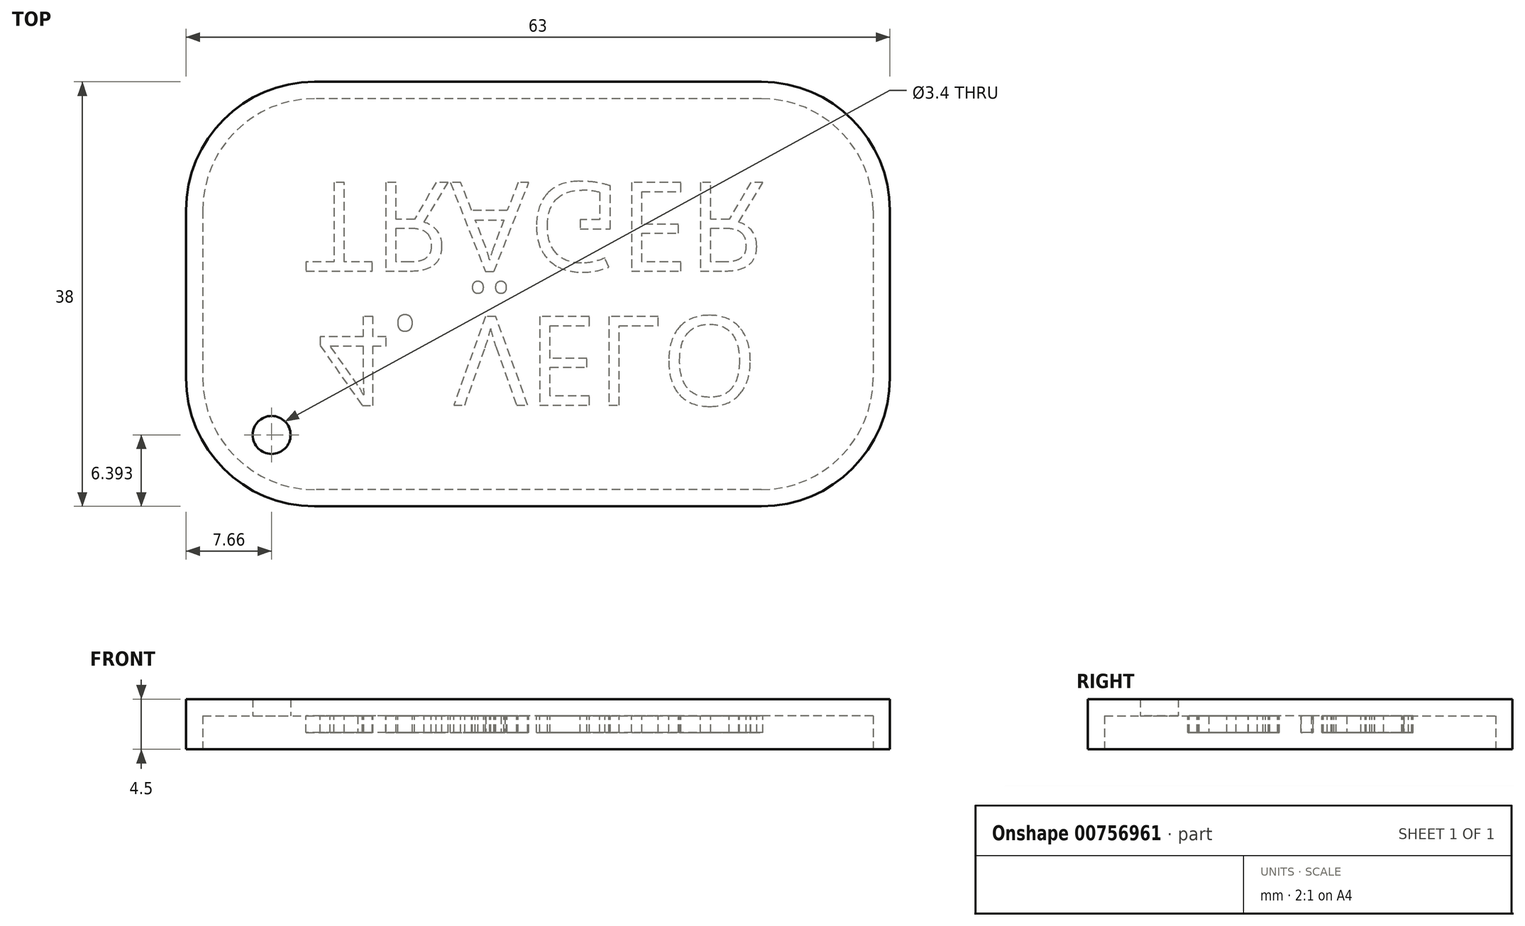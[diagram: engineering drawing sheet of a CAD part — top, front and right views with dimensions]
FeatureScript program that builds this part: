
annotation { "Feature Type Name" : "Feature", "Feature Type Description" : "" }
export const myFeature = defineFeature(function(context is Context, id is Id, definition is map)
    precondition{}
    {
        {
            var Q0;
            Q0=qCreatedBy(makeId("Top.planeOp"),FACE);
            var sketch = newSketch(context, id + "F0", { "sketchPlane" : qUnion([Q0])});
            skLineSegment(sketch, "E0.bottom", {"start": v(30, 17.5) * mm, "end": v(-30, 17.5) * mm});
            skLineSegment(sketch, "E0.top", {"start": v(30, -17.5) * mm, "end": v(-30, -17.5) * mm});
            skLineSegment(sketch, "E0.left", {"start": v(30, 17.5) * mm, "end": v(30, -17.5) * mm});
            skLineSegment(sketch, "E0.right", {"start": v(-30, 17.5) * mm, "end": v(-30, -17.5) * mm});
            skPoint(sketch, "E0.middle", {"position": v(0, 0) * mm});
            skSolve(sketch);
        }
        {
            var Q0;
            Q0=makeQuery(id+"F0.imprint","IMPRINT",FACE,{"disambiguationData":[TD([[makeQuery(id+"F0.imprint","IMPRINT",EDGE,{"derivedFrom":sQuery(id+"F0.wireOp",EDGE,"E0.bottom")}),1.0]])]});
            extrude(context, id + "F1", {"entities" : qUnion([Q0]), "depth" : 3 * mm, "offsetDistance" : 25 * mm});
        }
        {
            var Q0;
            Q0=makeQuery(id+"F1.opExtrude","SWEPT_EDGE",EDGE,{"disambiguationData":[OSD([sQuery(id+"F0.wireOp",EDGE,"E0.bottom"),sQuery(id+"F0.wireOp",EDGE,"E0.left")])]});
            var Q1;
            Q1=makeQuery(id+"F1.opExtrude","SWEPT_EDGE",EDGE,{"disambiguationData":[OSD([sQuery(id+"F0.wireOp",EDGE,"E0.top"),sQuery(id+"F0.wireOp",EDGE,"E0.right")])]});
            var Q2;
            Q2=makeQuery(id+"F1.opExtrude","SWEPT_EDGE",EDGE,{"disambiguationData":[OSD([sQuery(id+"F0.wireOp",EDGE,"E0.top"),sQuery(id+"F0.wireOp",EDGE,"E0.left")])]});
            var Q3;
            Q3=makeQuery(id+"F1.opExtrude","SWEPT_EDGE",EDGE,{"disambiguationData":[OSD([sQuery(id+"F0.wireOp",EDGE,"E0.bottom"),sQuery(id+"F0.wireOp",EDGE,"E0.right")])]});
            fillet(context, id + "F2", {"entities" : qUnion([Q0, Q1, Q2, Q3]), "radius" : 10 * mm, "tangentPropagation" : true, "allowEdgeOverflow" : false});
        }
        {
            var Q0;
            Q0=makeQuery(id+"F1.opExtrude","CAP_FACE",FACE,{"disambiguationData":[OSD([sQuery(id+"F0.wireOp",EDGE,"E0.bottom"),sQuery(id+"F0.wireOp",EDGE,"E0.top"),sQuery(id+"F0.wireOp",EDGE,"E0.left"),sQuery(id+"F0.wireOp",EDGE,"E0.right")])],"isStart":true});
            shell(context, id + "F3", {"entities" : qUnion([Q0]), "thickness" : 1.5 * mm, "oppositeDirection" : true});
        }
        {
            var Q0;
            Q0=makeQuery(id+"F3.opShell","OFFSET_FACE",FACE,{"disambiguationData":[OSD([sQuery(id+"F0.wireOp",EDGE,"E0.bottom"),sQuery(id+"F0.wireOp",EDGE,"E0.top"),sQuery(id+"F0.wireOp",EDGE,"E0.left"),sQuery(id+"F0.wireOp",EDGE,"E0.right")])]});
            var sketch = newSketch(context, id + "F4", { "sketchPlane" : qUnion([Q0])});
            skText(sketch, "E1", { "text": "TRÄGER", "fontName": "OpenSans-Regular.ttf"});
            skText(sketch, "E2", { "text": "4. VELO", "fontName": "OpenSans-Regular.ttf"});
            const initialGuessF4  = {"E1": [-0.02086, -0.01, 1, 0, 0.008], "E2": [-0.01973, 0.002, 1, 0, 0.008]};
            skSetInitialGuess(sketch, initialGuessF4);
            skSolve(sketch);
        }
        {
            var Q0;
            Q0=qSketchRegion(id+"F4",true);
            extrude(context, id + "F5", {"entities" : qUnion([Q0]), "operationType" : NewBodyOperationType.ADD, "depth" : 1.5 * mm, "offsetDistance" : 25 * mm});
        }
        {
            var Q0;
            {var subQ0=sQuery(id+"F0.wireOp",EDGE,"E0.right");var subQ1=sQuery(id+"F0.wireOp",EDGE,"E0.top");var subQ2=sQuery(id+"F0.wireOp",EDGE,"E0.left");var subQ3=sQuery(id+"F0.wireOp",EDGE,"E0.bottom");Q0=makeQuery(id+"F5.boolean.opBoolean","SPLIT",FACE,{"disambiguationData":[TD([makeQuery(id+"F3.opShell","OFFSET_FACE",FACE,{"disambiguationData":[OSD([subQ3])]})])],"derivedFrom":makeQuery(id+"F3.opShell","OFFSET_FACE",FACE,{"disambiguationData":[OSD([subQ3,subQ1,subQ2,subQ0])]})});}
            var sketch = newSketch(context, id + "F6", { "sketchPlane" : qUnion([Q0])});
            skPoint(sketch, "E3", {"position": v(-23.84, 12.6) * mm});
            skSolve(sketch);
        }
        {
            var Q0;
            Q0=sQuery(id+"F6.wireOp",VERTEX,"E3");
            var Q1;
            Q1=makeQuery(id+"F1.opExtrude","SWEPT_BODY",BODY,{"disambiguationData":[OSD([sQuery(id+"F0.wireOp",EDGE,"E0.bottom"),sQuery(id+"F0.wireOp",EDGE,"E0.top"),sQuery(id+"F0.wireOp",EDGE,"E0.left"),sQuery(id+"F0.wireOp",EDGE,"E0.right")])]});
            hole(context, id + "F7", {"style" : HoleStyle.SIMPLE, "endStyle" : HoleEndStyle.THROUGH, "holeDiameter" : 3.4 * mm, "majorDiameter" : 5 * mm, "isTappedThrough" : true, "tappedDepth" : 12 * mm, "tapClearance" : 3, "locations" : qUnion([Q0]), "scope" : qUnion([Q1])});
        }
    });
